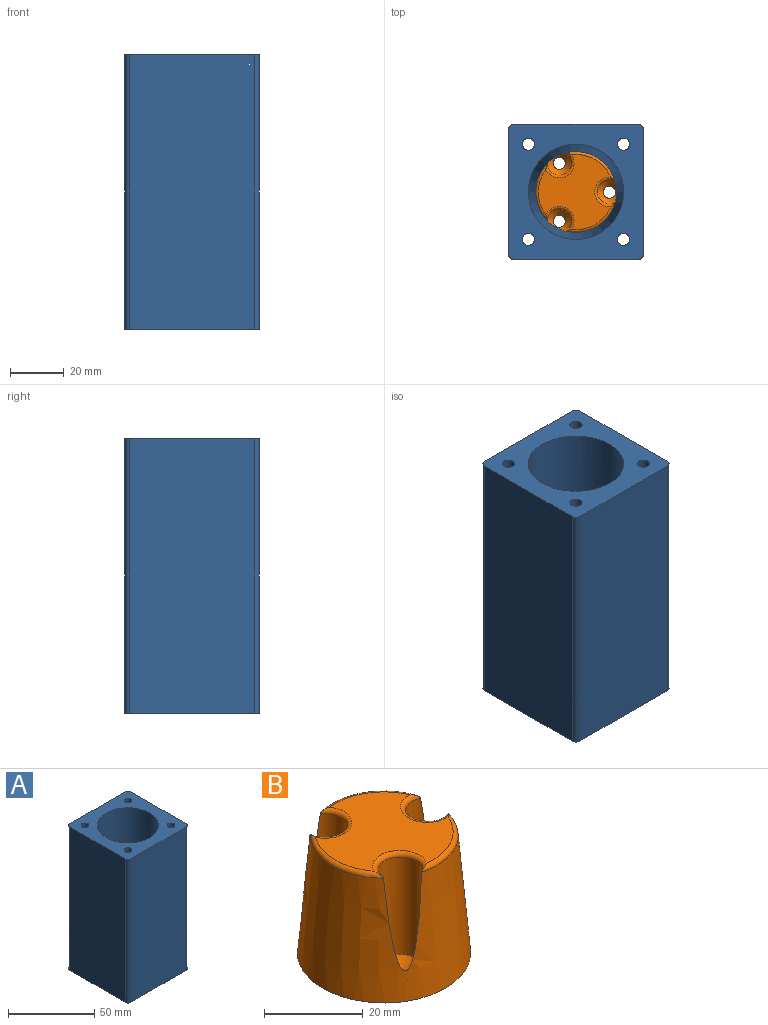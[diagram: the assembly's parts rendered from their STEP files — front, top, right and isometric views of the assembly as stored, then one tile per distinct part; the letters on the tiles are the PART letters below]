
ASSEMBLY  parts=2 mates=1
PART A: 25 faces, bbox 50x50x102 mm
  f0: plane 102x46mm, normal (0,-1,0), area 4692mm2, adj f4,f14,f17,f24
  f1: plane 102x46mm, normal (1,0,0), area 4692mm2, adj f4,f14,f15,f24
  f2: plane 102x46mm, normal (0,1,0), area 4692mm2, adj f4,f15,f16,f24
  f3: plane 102x46mm, normal (-1,0,0), area 4692mm2, adj f4,f16,f17,f24
  f4: plane 50x50mm, normal (0,0,1), area 1447.5mm2, adj f0,f1,f2,f3,f5,f7,f9,f11
  f5: cylinder r=2.25mm len=4.5mm, axis (0,0,-1), area 39.2mm2, adj f4,f6
  f6: cone r=2.25mm half-angle=45deg, axis (0,0,-1), area 66.7mm2, adj f5,f18
  f7: cylinder r=2.25mm len=4.5mm, axis (0,0,-1), area 39.2mm2, adj f4,f8
  f8: cone r=2.25mm half-angle=45deg, axis (0,0,-1), area 66.7mm2, adj f7,f19
  f9: cylinder r=2.25mm len=4.5mm, axis (0,0,-1), area 39.2mm2, adj f4,f10
  f10: cone r=2.25mm half-angle=45deg, axis (0,0,-1), area 66.7mm2, adj f9,f20
  f11: cylinder r=2.25mm len=4.5mm, axis (0,0,-1), area 39.2mm2, adj f4,f12
  f12: cone r=2.25mm half-angle=45deg, axis (0,0,-1), area 66.7mm2, adj f11,f21
  f13: cylinder r=17.71mm len=42mm, axis (0,0,-1), area 4673.8mm2, adj f4,f22
  f14: cylinder r=2mm len=102mm, axis (0,0,1), area 320.4mm2, adj f0,f1,f4,f24
  f15: cylinder r=2mm len=102mm, axis (0,0,-1), area 320.4mm2, adj f1,f2,f4,f24
  f16: cylinder r=2mm len=102mm, axis (0,0,1), area 320.4mm2, adj f2,f3,f4,f24
  f17: cylinder r=2mm len=102mm, axis (0,0,-1), area 320.4mm2, adj f0,f3,f4,f24
  f18: cylinder r=4.48mm len=97mm, axis (0,0,1), area 2730.4mm2, adj f6,f24
  f19: cylinder r=4.48mm len=97mm, axis (0,0,1), area 2730.4mm2, adj f8,f24
  f20: cylinder r=4.48mm len=97mm, axis (0,0,1), area 2730.4mm2, adj f10,f24
  f21: cylinder r=4.48mm len=97mm, axis (0,0,1), area 2730.4mm2, adj f12,f24
  f22: cone r=17.71mm half-angle=5deg, axis (0,0,1), area 3102.9mm2, adj f13,f23
  f23: cone r=17.71mm half-angle=5deg, axis (0,0,-1), area 3102.9mm2, adj f22,f24
  f24: plane 50x50mm, normal (0,0,-1), area 1258.9mm2, adj f0,f1,f2,f3,f14,f15,f16,f17
PART B: 18 faces, bbox 35x35x30 mm
  f0: cone r=17.51mm half-angle=5deg, axis (0,0,-1), area 2601.3mm2, adj f2,f3,f6,f9,f12,f13,f14,f15
  f1: plane 27.94x26.83mm, normal (0,0,1), area 432.2mm2, adj f12,f13,f14,f15,f16,f17
  f2: plane 35.02x35.02mm, normal (0,0,-1), area 915.6mm2, adj f0,f4,f7,f10
  f3: cylinder r=4.48mm len=24mm, axis (0,0,-1), area 533.6mm2, adj f0,f5,f13
  f4: cylinder r=2.25mm len=4.5mm, axis (0,0,1), area 39.2mm2, adj f2,f5
  f5: cone r=2.25mm half-angle=45deg, axis (0,0,1), area 66.7mm2, adj f3,f4
  f6: cylinder r=4.48mm len=24mm, axis (0,0,-1), area 534.7mm2, adj f0,f8,f14
  f7: cylinder r=2.25mm len=4.5mm, axis (0,0,1), area 39.2mm2, adj f2,f8
  f8: cone r=2.25mm half-angle=45deg, axis (0,0,1), area 66.7mm2, adj f6,f7
  f9: cylinder r=4.48mm len=24mm, axis (0,0,-1), area 533.2mm2, adj f0,f11,f17
  f10: cylinder r=2.25mm len=4.5mm, axis (0,0,1), area 39.2mm2, adj f2,f11
  f11: cone r=2.25mm half-angle=45deg, axis (0,0,1), area 66.7mm2, adj f9,f10
  f12: torus R=13.97mm, axis (0,0,1), area 31.4mm2, adj f0,f1,f13,f14
  f13: torus R=5.48mm, axis (0,0,1), area 28.6mm2, adj f0,f1,f3,f12,f15
  f14: torus R=5.48mm, axis (0,0,1), area 28.6mm2, adj f0,f1,f6,f12,f16
  f15: torus R=13.97mm, axis (0,0,1), area 31.4mm2, adj f0,f1,f13,f17
  f16: torus R=13.97mm, axis (0,0,1), area 31.4mm2, adj f0,f1,f14,f17
  f17: torus R=5.48mm, axis (0,0,1), area 28.6mm2, adj f0,f1,f9,f15,f16
PLACE A t=(28,20.71,148.9)mm
PLACE B t=(28,20.71,51.9)mm
MATE revolute A.f13 <-> B.f0  axis (0,0,-1) through (28,20.71,51.9)mm
